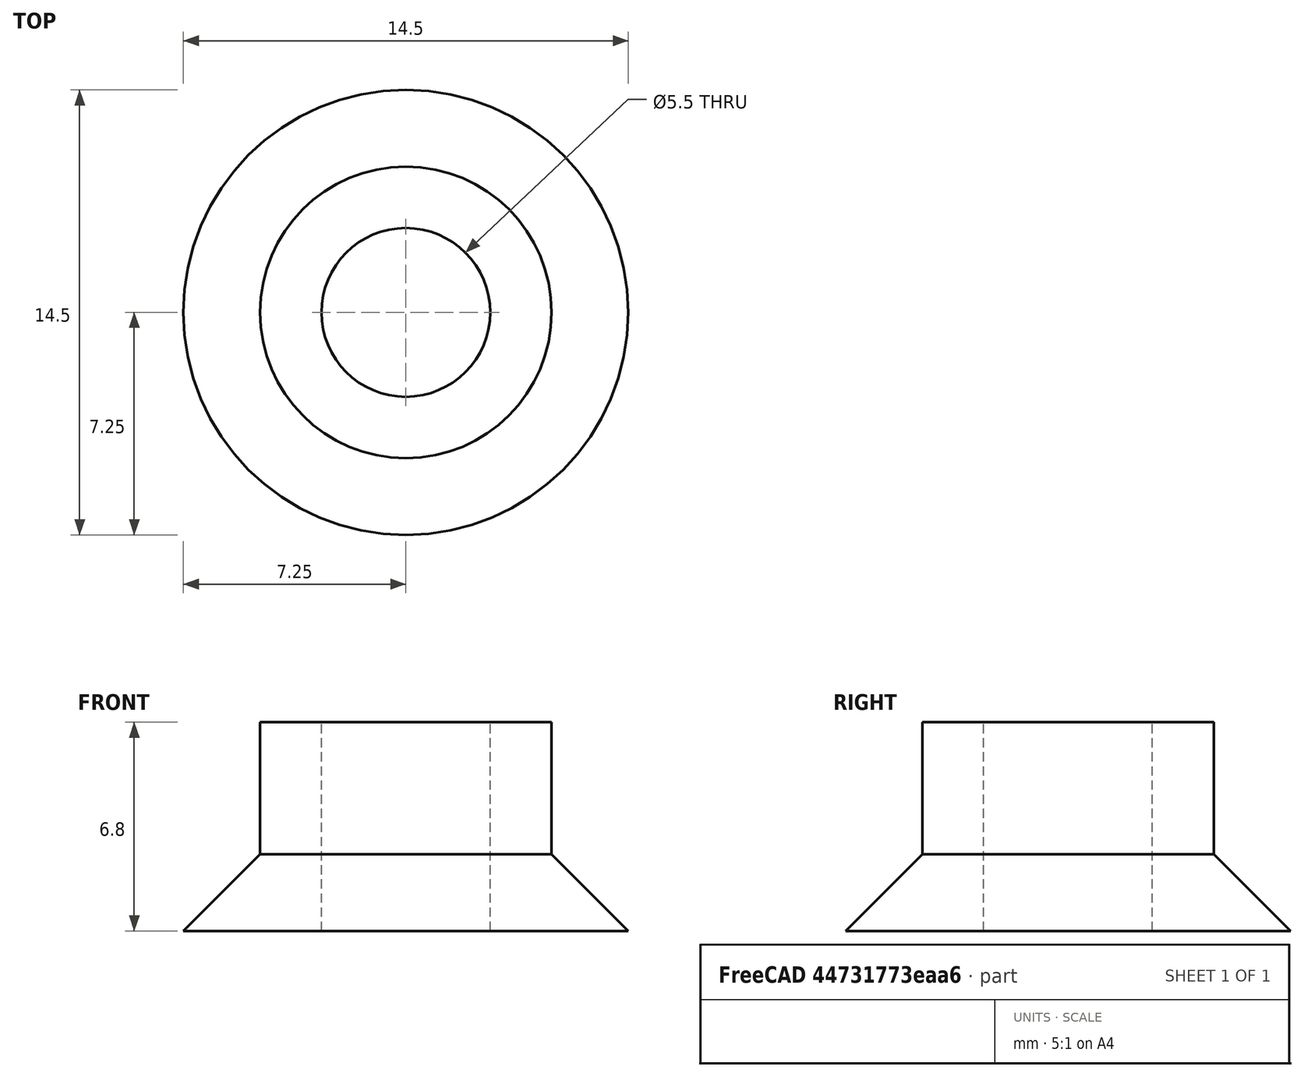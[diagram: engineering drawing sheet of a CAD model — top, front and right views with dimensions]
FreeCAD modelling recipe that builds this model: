
FCSTD DOCUMENT  (FreeCAD 0.19R24267 +148 (Git))
Label: Roller spacer
License: All rights reserved
LicenseURL: http://en.wikipedia.org/wiki/All_rights_reserved
objects: Sketcher::SketchObject×1, PartDesign::Revolution×1, PartDesign::Body×1
note: 4 computed .brp shape members not serialized (recipe doc carries the construction recipe); baked Part::Feature solids carry a one-line shape summary decoded from their .brp

FEATURE [Sketcher::SketchObject] Sketch
  FullyConstrained = false
  MapMode = 5
  Placement = pos=(0,0,0) rot=(1,0,0;1.5708rad)
  Support = -> [XZ_Plane]
  sketch-geometry (7):
    g0: LineSegment StartX=2.75 StartY=0 StartZ=0 EndX=2.75 EndY=6.8 EndZ=0
    g1: LineSegment StartX=2.75 StartY=6.8 StartZ=0 EndX=4.75 EndY=6.8 EndZ=0
    g2: LineSegment StartX=4.75 StartY=6.8 StartZ=0 EndX=4.75 EndY=2.5 EndZ=0
    g3: LineSegment StartX=4.75 StartY=2.5 StartZ=0 EndX=7.25 EndY=0 EndZ=0
    g4: LineSegment StartX=2.75 StartY=0 StartZ=0 EndX=7.25 EndY=0 EndZ=0
    g5: LineSegment StartX=2.75 StartY=0 StartZ=0 EndX=0 EndY=0 EndZ=0
    g6: LineSegment StartX=0 StartY=0 StartZ=0 EndX=0 EndY=8.34893 EndZ=0
  constraints (19):
    c: PointOnObject(g0,g-1)
    c: Vertical(g0)
    c: Horizontal(g1)
    c: Coincident(g2,g1)
    c: Vertical(g2)
    c: Coincident(g3,g2)
    c: PointOnObject(g3,g-1)
    c: Coincident(g4,g0)
    c: Coincident(g4,g3)
    c: Coincident(g5,g0)
    c: Coincident(g5,g-1)
    c: DistanceX(g5,g5) = 2.75
    c: Coincident(g1,g0)
    c: DistanceX(g1,g1) = 2
    c: Angle(g3,g2) = 2.35619
    c: DistanceX(g2,g3) = 2.5
    c: DistanceY(g0,g0) = 6.8
    c: Coincident(g6,g-1)
    c: PointOnObject(g6,g-2)
FEATURE [PartDesign::Revolution] Revolution
  Angle = 360
  Axis = (0,-2e-16,1)
  Base = (0,0,0)
  Placement = pos=(0,0,0) rot=(1,0,0;1.5708rad)
  Profile = -> Sketch
  ReferenceAxis = -> Sketch [V_Axis]
  Reversed = true
FEATURE [PartDesign::Body] Body
  Group = -> [Sketch,Revolution]
  Origin = -> Origin
  Tip = -> Revolution
